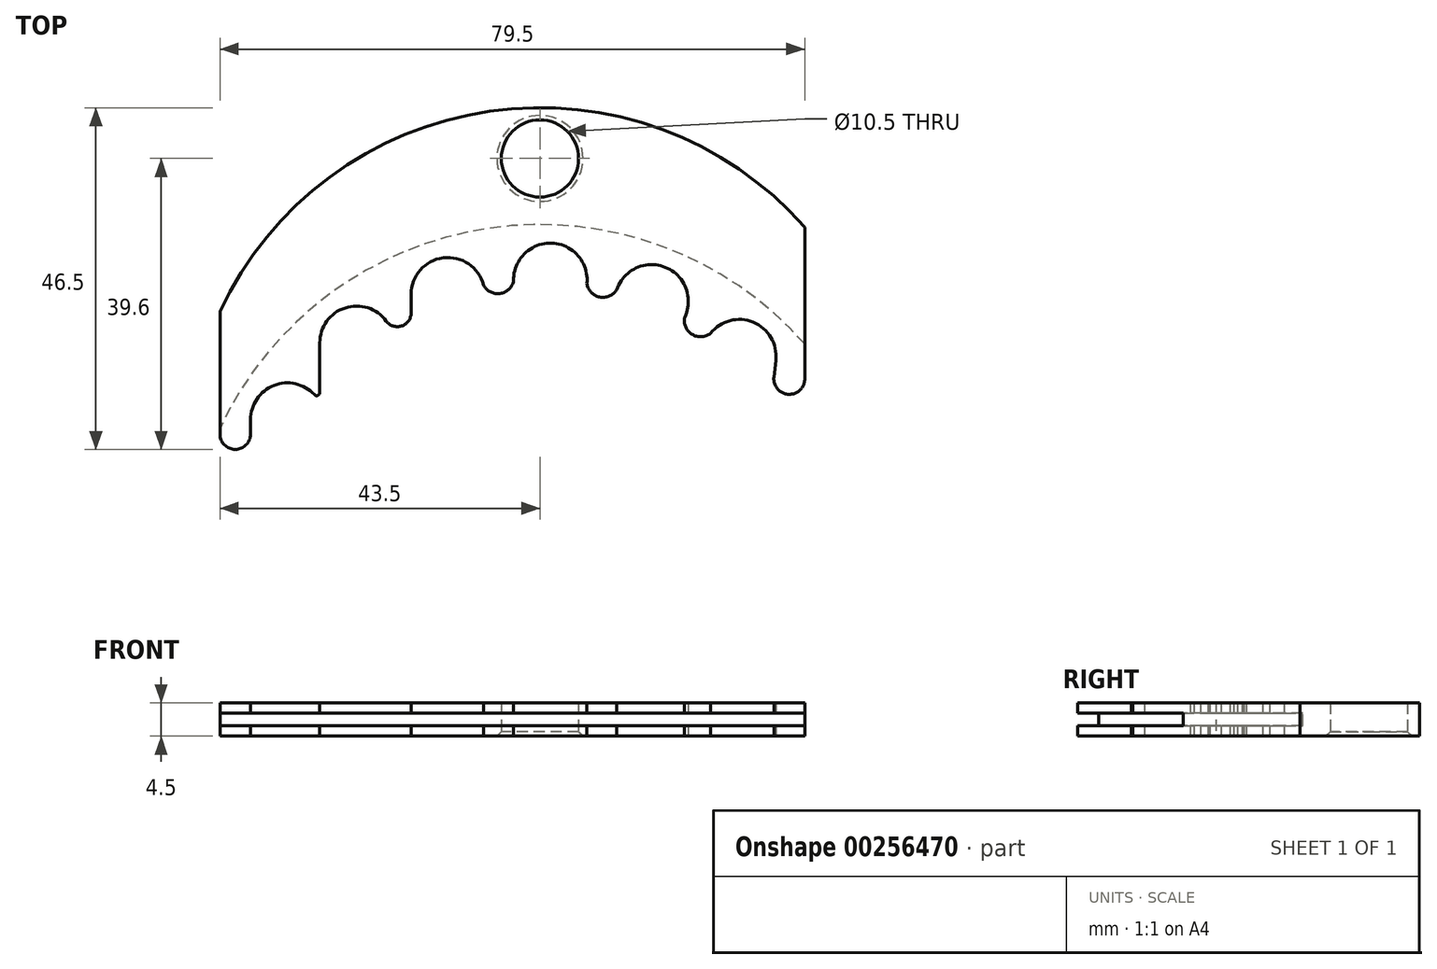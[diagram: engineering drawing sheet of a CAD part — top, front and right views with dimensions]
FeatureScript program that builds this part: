
annotation { "Feature Type Name" : "Feature", "Feature Type Description" : "" }
export const myFeature = defineFeature(function(context is Context, id is Id, definition is map)
    precondition{}
    {
        {
            var Q0;
            Q0=qCreatedBy(makeId("Top.planeOp"),FACE);
            var sketch = newSketch(context, id + "F0", { "sketchPlane" : qUnion([Q0])});
            skCircle(sketch, "E0", {"center": v(0, 0) * mm, "radius": 13 * mm, "construction": true});
            skCircle(sketch, "E1", {"center": v(0, 0) * mm, "radius": 13.5 * mm, "construction": true});
            skCircle(sketch, "E2", {"center": v(0, 0) * mm, "radius": 16 * mm, "construction": true});
            skLineSegment(sketch, "E3", {"start": v(0, 0) * mm, "end": v(0.47, 13.5) * mm, "construction": true});
            skLineSegment(sketch, "E4", {"start": v(0, 0) * mm, "end": v(5.06, 12.52) * mm, "construction": true});
            skLineSegment(sketch, "E5", {"start": v(0, 0) * mm, "end": v(9.03, 10.03) * mm, "construction": true});
            skLineSegment(sketch, "E6", {"start": v(0, 0) * mm, "end": v(-4.17, 12.84) * mm, "construction": true});
            skLineSegment(sketch, "E7", {"start": v(0, 0) * mm, "end": v(-8.31, 10.64) * mm, "construction": true});
            skLineSegment(sketch, "E8", {"start": v(0, 0) * mm, "end": v(-11.45, 7.15) * mm, "construction": true});
            skArc(sketch, "E9", {"start": v(2.13, 13.33) * mm, "mid": v(0.53, 15.16) * mm, "end": v(-1.2, 13.45) * mm});
            skArc(sketch, "E10", {"start": v(6.56, 11.8) * mm, "mid": v(5.68, 14.06) * mm, "end": v(3.48, 13.04) * mm});
            skArc(sketch, "E11", {"start": v(10.69, 9.85) * mm, "mid": v(9.67, 11.57) * mm, "end": v(7.73, 11.07) * mm});
            skArc(sketch, "E12", {"start": v(-2.56, 13.26) * mm, "mid": v(-4.38, 14.5) * mm, "end": v(-5.84, 12.84) * mm});
            skArc(sketch, "E13", {"start": v(-6.94, 11.58) * mm, "mid": v(-8.8, 12.23) * mm, "end": v(-9.98, 10.64) * mm});
            skArc(sketch, "E14", {"start": v(-10.23, 8.29) * mm, "mid": v(-12.06, 8.7) * mm, "end": v(-13.12, 7.15) * mm});
            skArc(sketch, "E15", {"start": v(-2.56, 13.26) * mm, "mid": v(-1.8, 12.87) * mm, "end": v(-1.2, 13.45) * mm});
            skArc(sketch, "E16", {"start": v(2.13, 13.33) * mm, "mid": v(2.7, 12.72) * mm, "end": v(3.48, 13.04) * mm});
            skArc(sketch, "E17", {"start": v(6.56, 11.8) * mm, "mid": v(6.89, 11.02) * mm, "end": v(7.73, 11.07) * mm});
            skLineSegment(sketch, "E18", {"start": v(-5.84, 12.84) * mm, "end": v(-5.84, 12) * mm});
            skLineSegment(sketch, "E19", {"start": v(-6.97, 11.62) * mm, "end": v(-6.97, 11.62) * mm});
            skArc(sketch, "E20", {"start": v(-6.97, 11.62) * mm, "mid": v(-6.27, 11.4) * mm, "end": v(-5.84, 12) * mm});
            skLineSegment(sketch, "E21", {"start": v(-9.98, 10.64) * mm, "end": v(-9.98, 8.38) * mm});
            skArc(sketch, "E22", {"start": v(-10.23, 8.29) * mm, "mid": v(-10.07, 8.25) * mm, "end": v(-9.98, 8.38) * mm});
            skArc(sketch, "E23", {"start": v(-14.5, 6.5) * mm, "mid": v(-13.8, 5.8) * mm, "end": v(-13.12, 6.5) * mm});
            skArc(sketch, "E24", {"start": v(10.6, 9.08) * mm, "mid": v(11.26, 8.3) * mm, "end": v(12, 9) * mm});
            skLineSegment(sketch, "E25", {"start": v(-14.5, 0) * mm, "end": v(-14.5, 12.06) * mm});
            skLineSegment(sketch, "E26", {"start": v(12, 0) * mm, "end": v(12, 15.88) * mm});
            skArc(sketch, "E27", {"start": v(12, 15.88) * mm, "mid": v(-2.28, 21.14) * mm, "end": v(-14.5, 12.06) * mm});
            skLineSegment(sketch, "E28", {"start": v(-13.12, 7.15) * mm, "end": v(-13.12, 6.5) * mm});
            skLineSegment(sketch, "E29", {"start": v(-14.5, 19) * mm, "end": v(12, 19) * mm, "construction": true});
            skLineSegment(sketch, "E30", {"start": v(10.69, 9.85) * mm, "end": v(10.6, 9.08) * mm});
            skCircle(sketch, "E31", {"center": v(0, 19) * mm, "radius": 1.75 * mm});
            skSolve(sketch);
        }
        {
            var Q0;
            Q0=makeQuery(id+"F0.imprint","IMPRINT",FACE,{"disambiguationData":[TD([[makeQuery(id+"F0.imprint","IMPRINT",EDGE,{"derivedFrom":sQuery(id+"F0.wireOp",EDGE,"E9")}),-1.0]])]});
            extrude(context, id + "F1", {"entities" : qUnion([Q0]), "depth" : 1.5 * mm, "symmetric" : true});
        }
        {
            var Q0;
            Q0=makeQuery(id+"F1.opExtrude","CAP_EDGE",EDGE,{"disambiguationData":[OSD([sQuery(id+"F0.wireOp",EDGE,"E31")])],"isStart":true});
            chamfer(context, id + "F2", {"entities" : qUnion([Q0]), "width" : 0.2 * mm, "tangentPropagation" : true});
        }
        {
            var Q0;
            Q0=qCreatedBy(makeId("Top.planeOp"),FACE);
            var sketch = newSketch(context, id + "F3", { "sketchPlane" : qUnion([Q0])});
            skCircle(sketch, "E32", {"center": v(0, 0) * mm, "radius": 16 * mm});
            skSolve(sketch);
        }
        {
            var Q0;
            Q0=makeQuery(id+"F3.imprint","IMPRINT",FACE,{"disambiguationData":[TD([[makeQuery(id+"F3.imprint","IMPRINT",EDGE,{"derivedFrom":sQuery(id+"F3.wireOp",EDGE,"E32")}),1.0]])]});
            extrude(context, id + "F4", {"entities" : qUnion([Q0]), "operationType" : NewBodyOperationType.REMOVE, "oppositeDirection" : true, "depth" : (0.5 + (0.1 + 0.09) / 3) * mm, "symmetric" : true});
        }
        {
            var Q0;
            Q0=makeQuery(id+"F1.opExtrude","SWEPT_BODY",BODY,{"disambiguationData":[OSD([sQuery(id+"F0.wireOp",EDGE,"E9"),sQuery(id+"F0.wireOp",EDGE,"E10"),sQuery(id+"F0.wireOp",EDGE,"E11"),sQuery(id+"F0.wireOp",EDGE,"E12"),sQuery(id+"F0.wireOp",EDGE,"E13"),sQuery(id+"F0.wireOp",EDGE,"E14"),sQuery(id+"F0.wireOp",EDGE,"E15"),sQuery(id+"F0.wireOp",EDGE,"E16"),sQuery(id+"F0.wireOp",EDGE,"E17"),sQuery(id+"F0.wireOp",EDGE,"E18"),sQuery(id+"F0.wireOp",EDGE,"E20"),sQuery(id+"F0.wireOp",EDGE,"E21"),sQuery(id+"F0.wireOp",EDGE,"E22"),sQuery(id+"F0.wireOp",EDGE,"E23"),sQuery(id+"F0.wireOp",EDGE,"E24"),sQuery(id+"F0.wireOp",EDGE,"E25"),sQuery(id+"F0.wireOp",EDGE,"E26"),sQuery(id+"F0.wireOp",EDGE,"E27"),sQuery(id+"F0.wireOp",EDGE,"E28"),sQuery(id+"F0.wireOp",EDGE,"E30"),sQuery(id+"F0.wireOp",EDGE,"E31")])]});
            var Q1;
            Q1=qCreatedBy(makeId("Origin.pointOp"),VERTEX);
            transform(context, id + "F5", {"entities" : qUnion([Q0]), "transformType" : TransformType.SCALE_UNIFORMLY, "scale" : 3, "makeCopy" : false, "scalePoint" : qUnion([Q1])});
        }
    });
